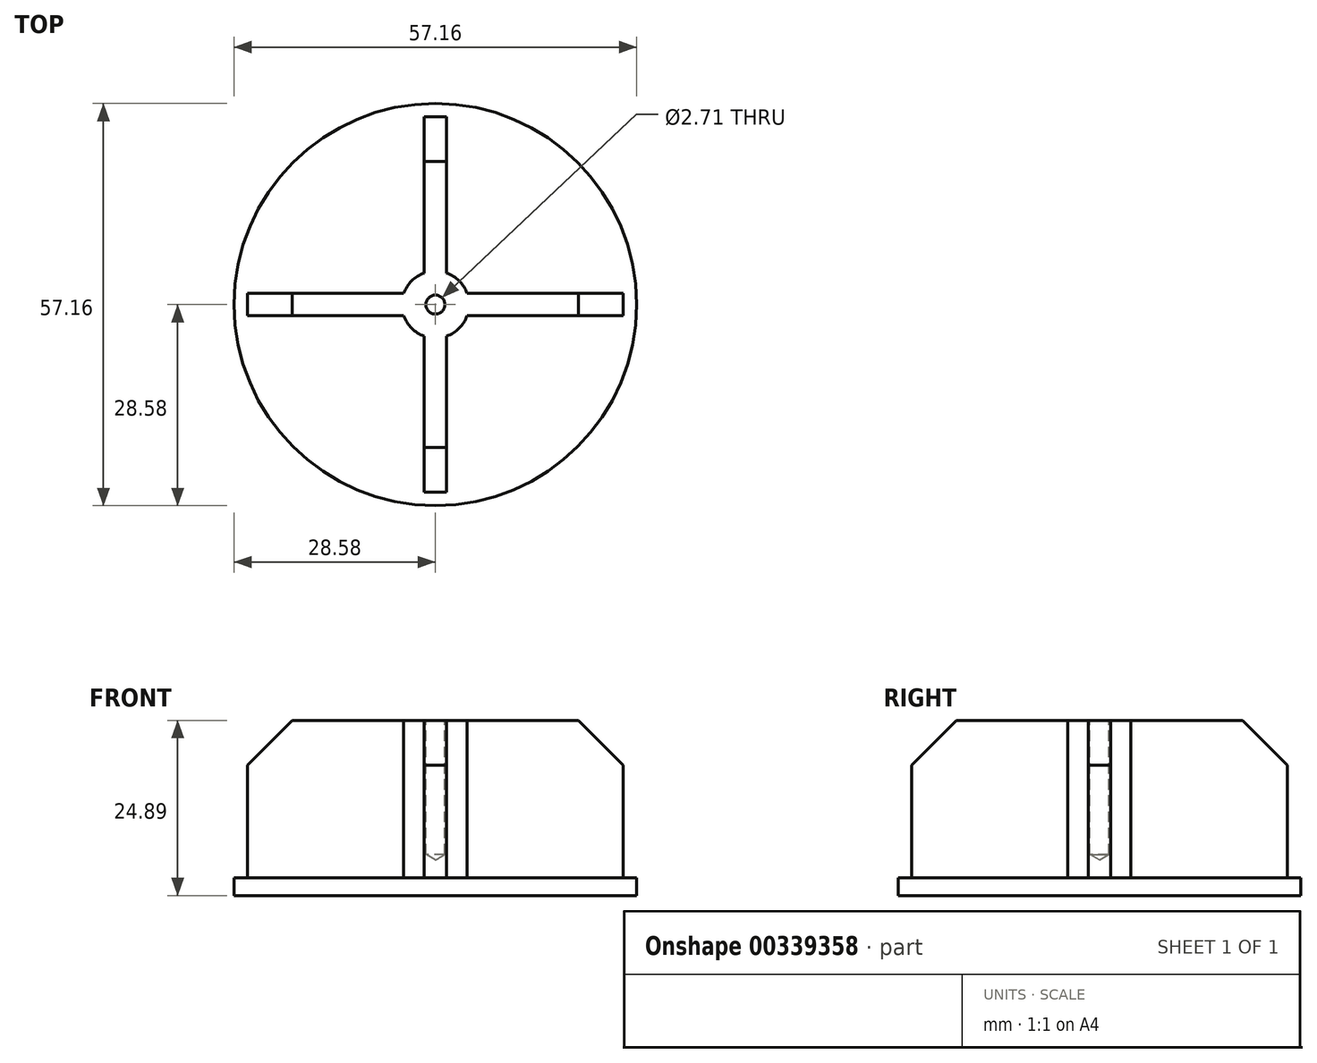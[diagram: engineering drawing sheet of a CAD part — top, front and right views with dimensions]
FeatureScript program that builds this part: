
annotation { "Feature Type Name" : "Feature", "Feature Type Description" : "" }
export const myFeature = defineFeature(function(context is Context, id is Id, definition is map)
    precondition{}
    {
        {
            var Q0;
            Q0=qCreatedBy(makeId("Top.planeOp"),FACE);
            var sketch = newSketch(context, id + "F0", { "sketchPlane" : qUnion([Q0])});
            skCircle(sketch, "E0", {"center": v(0, 0) * mm, "radius": 28.58 * mm});
            skSolve(sketch);
        }
        {
            var Q0;
            Q0=qSketchRegion(id+"F0",true);
            extrude(context, id + "F1", {"entities" : qUnion([Q0]), "depth" : 2.54 * mm});
        }
        {
            var Q0;
            Q0=makeQuery(id+"F1.opExtrude","CAP_FACE",FACE,{"disambiguationData":[OSD([sQuery(id+"F0.wireOp",EDGE,"E0")])],"isStart":false});
            var sketch = newSketch(context, id + "F2", { "sketchPlane" : qUnion([Q0])});
            skLineSegment(sketch, "E1.bottom", {"start": v(26.67, 1.59) * mm, "end": v(1.59, 1.59) * mm});
            skLineSegment(sketch, "E1.top", {"start": v(26.67, -1.59) * mm, "end": v(1.59, -1.59) * mm});
            skLineSegment(sketch, "E1.left", {"start": v(26.67, 1.59) * mm, "end": v(26.67, -1.59) * mm});
            skLineSegment(sketch, "E1.right", {"start": v(-26.67, 1.59) * mm, "end": v(-26.67, -1.59) * mm});
            skPoint(sketch, "E1.middle", {"position": v(0, 0) * mm});
            skLineSegment(sketch, "E2.bottom", {"start": v(1.59, 26.67) * mm, "end": v(-1.59, 26.67) * mm});
            skLineSegment(sketch, "E2.top", {"start": v(1.59, -26.67) * mm, "end": v(-1.59, -26.67) * mm});
            skLineSegment(sketch, "E2.left", {"start": v(1.59, 26.67) * mm, "end": v(1.59, 1.59) * mm});
            skLineSegment(sketch, "E2.right", {"start": v(-1.59, 26.67) * mm, "end": v(-1.59, 1.59) * mm});
            skLineSegment(sketch, "E3.trimOffspring", {"start": v(-1.59, -1.59) * mm, "end": v(-26.67, -1.59) * mm});
            skLineSegment(sketch, "E4.trimOffspring", {"start": v(-1.59, -1.59) * mm, "end": v(-1.59, -26.67) * mm});
            skLineSegment(sketch, "E5.trimOffspring", {"start": v(-1.59, 1.59) * mm, "end": v(-26.67, 1.59) * mm});
            skLineSegment(sketch, "E6.trimOffspring", {"start": v(1.59, -1.59) * mm, "end": v(1.59, -26.67) * mm});
            skSolve(sketch);
        }
        {
            var Q0;
            Q0=qSketchRegion(id+"F2",true);
            extrude(context, id + "F3", {"entities" : qUnion([Q0]), "operationType" : NewBodyOperationType.ADD, "depth" : 22.35 * mm});
        }
        {
            var Q0;
            Q0=makeQuery(id+"F3.opExtrude","CAP_EDGE",EDGE,{"disambiguationData":[OSD([sQuery(id+"F2.wireOp",EDGE,"E2.top")])],"isStart":false});
            var Q1;
            Q1=makeQuery(id+"F3.opExtrude","CAP_EDGE",EDGE,{"disambiguationData":[OSD([sQuery(id+"F2.wireOp",EDGE,"E1.left")])],"isStart":false});
            var Q2;
            Q2=makeQuery(id+"F3.opExtrude","CAP_EDGE",EDGE,{"disambiguationData":[OSD([sQuery(id+"F2.wireOp",EDGE,"E2.bottom")])],"isStart":false});
            var Q3;
            Q3=makeQuery(id+"F3.opExtrude","CAP_EDGE",EDGE,{"disambiguationData":[OSD([sQuery(id+"F2.wireOp",EDGE,"E1.right")])],"isStart":false});
            chamfer(context, id + "F4", {"entities" : qUnion([Q0, Q1, Q2, Q3]), "width" : 6.35 * mm, "tangentPropagation" : true});
        }
        {
            var Q0;
            Q0=makeQuery(id+"F3.opExtrude","CAP_FACE",FACE,{"disambiguationData":[OSD([sQuery(id+"F2.wireOp",EDGE,"E1.bottom"),sQuery(id+"F2.wireOp",EDGE,"E1.top"),sQuery(id+"F2.wireOp",EDGE,"E1.left"),sQuery(id+"F2.wireOp",EDGE,"E1.right"),sQuery(id+"F2.wireOp",EDGE,"E2.bottom"),sQuery(id+"F2.wireOp",EDGE,"E2.top"),sQuery(id+"F2.wireOp",EDGE,"E2.left"),sQuery(id+"F2.wireOp",EDGE,"E2.right"),sQuery(id+"F2.wireOp",EDGE,"E3.trimOffspring"),sQuery(id+"F2.wireOp",EDGE,"E4.trimOffspring"),sQuery(id+"F2.wireOp",EDGE,"E5.trimOffspring"),sQuery(id+"F2.wireOp",EDGE,"E6.trimOffspring")])],"isStart":false});
            var sketch = newSketch(context, id + "F5", { "sketchPlane" : qUnion([Q0])});
            skCircle(sketch, "E7", {"center": v(0, 0) * mm, "radius": 4.76 * mm});
            skSolve(sketch);
        }
        {
            var Q0;
            Q0=qSketchRegion(id+"F5",true);
            var Q1;
            Q1=makeQuery(id+"F1.opExtrude","CAP_FACE",FACE,{"disambiguationData":[OSD([sQuery(id+"F0.wireOp",EDGE,"E0")])],"isStart":false});
            extrude(context, id + "F6", {"entities" : qUnion([Q0]), "operationType" : NewBodyOperationType.ADD, "endBound" : BoundingType.UP_TO_SURFACE, "oppositeDirection" : true, "endBoundEntityFace" : qUnion([Q1]), "depth" : 25.4 * mm});
        }
        {
            var Q0;
            Q0=makeQuery(id+"F6.boolean.opBoolean","MERGE",FACE,{"derivedFrom":[makeQuery(id+"F3.opExtrude","CAP_FACE",FACE,{"disambiguationData":[OSD([sQuery(id+"F2.wireOp",EDGE,"E1.bottom"),sQuery(id+"F2.wireOp",EDGE,"E1.top"),sQuery(id+"F2.wireOp",EDGE,"E1.left"),sQuery(id+"F2.wireOp",EDGE,"E1.right"),sQuery(id+"F2.wireOp",EDGE,"E2.bottom"),sQuery(id+"F2.wireOp",EDGE,"E2.top"),sQuery(id+"F2.wireOp",EDGE,"E2.left"),sQuery(id+"F2.wireOp",EDGE,"E2.right"),sQuery(id+"F2.wireOp",EDGE,"E3.trimOffspring"),sQuery(id+"F2.wireOp",EDGE,"E4.trimOffspring"),sQuery(id+"F2.wireOp",EDGE,"E5.trimOffspring"),sQuery(id+"F2.wireOp",EDGE,"E6.trimOffspring")])],"isStart":false}),makeQuery(id+"F6.opExtrude","CAP_FACE",FACE,{"disambiguationData":[OSD([sQuery(id+"F5.wireOp",EDGE,"E7")])],"isStart":true})]});
            var sketch = newSketch(context, id + "F7", { "sketchPlane" : qUnion([Q0])});
            skPoint(sketch, "E8", {"position": v(0, 0) * mm});
            skSolve(sketch);
        }
        {
            var Q0;
            Q0=sQuery(id+"F7.wireOp",VERTEX,"E8");
            var Q1;
            Q1=makeQuery(id+"F1.opExtrude","SWEPT_BODY",BODY,{"disambiguationData":[OSD([sQuery(id+"F0.wireOp",EDGE,"E0")])]});
            hole(context, id + "F8", {"style" : HoleStyle.SIMPLE, "endStyle" : HoleEndStyle.BLIND, "standardTappedOrClearance" : lookupTablePath({ "standard" : "ANSI", "engagement" : "75%", "pitch" : "32 tpi", "size" : "#6", "type" : "Tapped" }), "standardBlindInLast" : lookupTablePath({ "standard" : "ANSI", "engagement" : "75%", "pitch" : "32 tpi", "size" : "#6", "type" : "Tapped" }), "holeDiameter" : 2.7 * mm, "showTappedDepth" : true, "holeDepth" : 19.05 * mm, "tappedDepth" : 16.67 * mm, "tapClearance" : 3, "locations" : qUnion([Q0]), "scope" : qUnion([Q1]), "majorDiameter" : 3.5 * mm});
        }
    });
